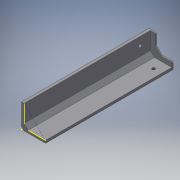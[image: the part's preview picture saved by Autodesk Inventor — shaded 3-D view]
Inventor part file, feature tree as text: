
AUTODESK INVENTOR PART (.ipt)
format: ipt  version: 2018 (Build 220112000, 112)  size: 192,000 bytes
history: native  units: in
note: dims shown in document units (in); Inventor stores cm internally (conversion verified against a paired STEP export)
features: sketch x8, extrude x3, hole x3, plane x1, fillet x1
ambient origin geometry x8: Origin, YZ Plane, XZ Plane, XY Plane, X Axis, Y Axis, Z Axis, Center Point
bodies: Solid1 (feature_tree)
feature tree (16):
  extrude  "Extrusion1"  Depth=0.75in
  extrude  "Extrusion2"  Depth=0.08in
  plane  "Work Plane1"
  extrude  "Extrusion4"  Depth=4.0in TaperAngle=0.0deg
  sketch  "Sketch6"  dims[d11=0.23in d15=0.23in d16=180.0deg]
  hole  "Hole1"  [1 undecoded]
  fillet  "Fillet1"  [1 undecoded]
  hole  "Hole2"  [1 undecoded]
  hole  "Hole3"  [1 undecoded]
  sketch  "Sketch10"  dims[d37=0.05in d38=0.6in d39=180.0deg d40=0.25in d41=0.4in d42=0.25in d43=0.5in d44=0.2in d45=0.0in d46=0.25in d47=0.25in d48=0.75in d49=0.375in d50=0.25in d51=0.5635in d52=1.0in d53=0.8108in d54=0.05in d55=0.2in d56=0.45in d57=0.1in d58=0.75in d59=0.375in d60=0.25in d61=0.5635in d62=1.0in d63=0.8108in d64=0.2in d65=0.45in d66=0.1in d67=0.75in d68=0.375in d69=0.25in d70=0.5635in d71=1.0in d72=0.8108in d73=0.1in d74=0.6793in d75=0.4in]
  sketch  "Sketch1"  dims[d0=0.75in d1=0.75in]
  sketch  "Sketch2"  dims[d2=0.08in d3=0.08in]
  sketch  "Sketch5"  dims[d8=0.15in d9=4.0in d10=0.0in]
  sketch  "Sketch7"  dims[d18=90.0deg d20=45.0deg]
  sketch  "Sketch8"  dims[d21=0.4in d22=0.04in d23=0.0in]
  sketch  "Sketch9"  dims[d30=0.5in]
note: 4 required parameter values undecoded (feature->parameter linkage not recoverable at this tier; creation-order binding heuristic only, values carry confidence <= 0.55)
